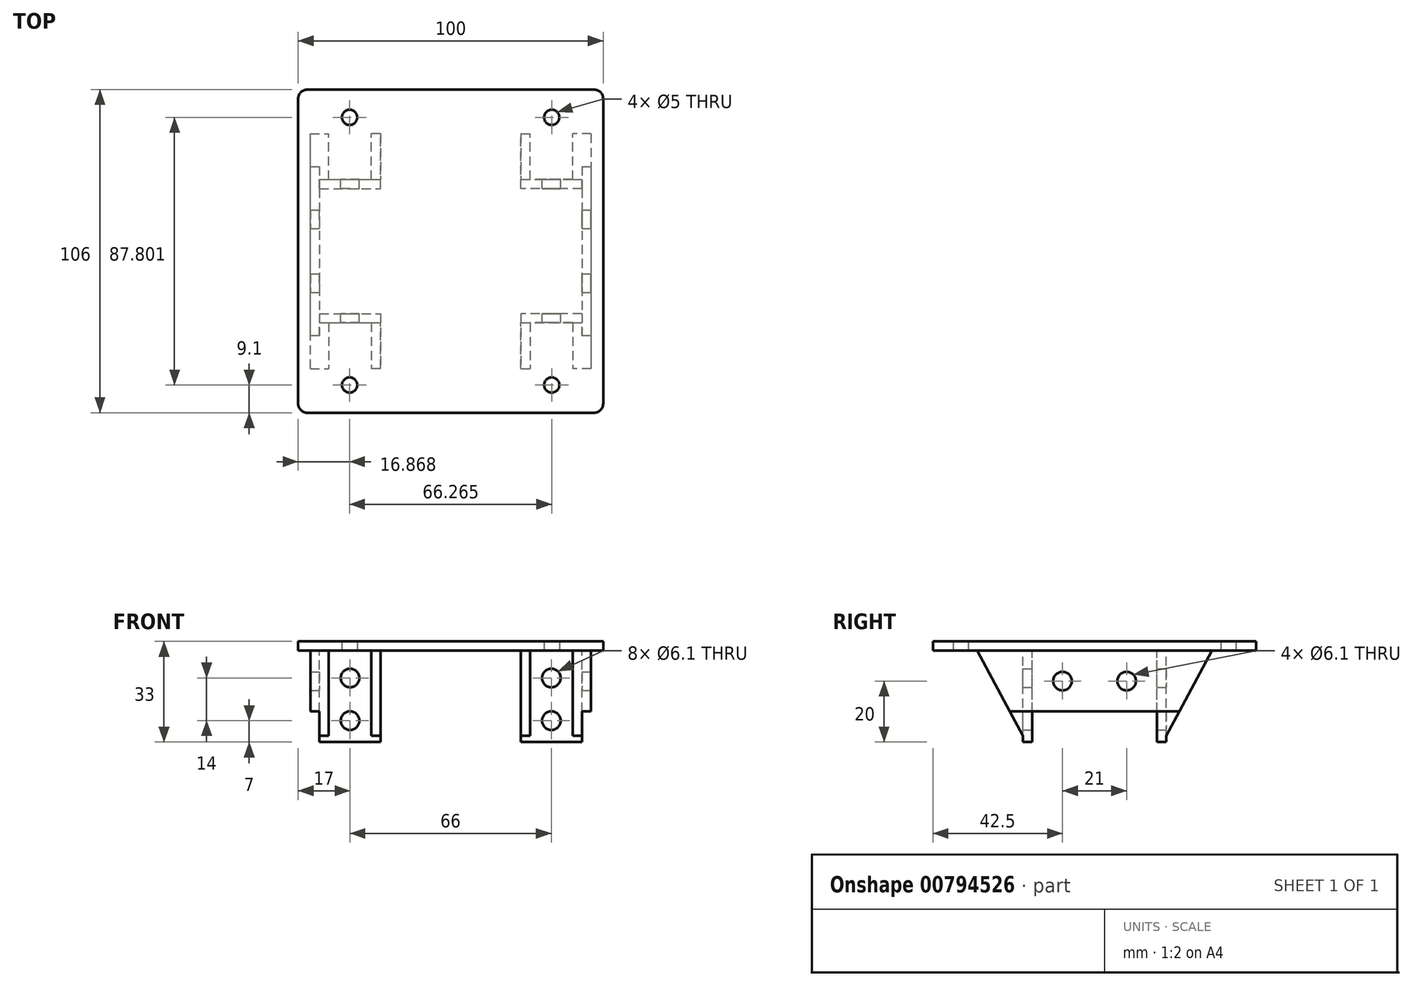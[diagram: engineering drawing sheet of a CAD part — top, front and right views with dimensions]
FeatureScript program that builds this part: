
annotation { "Feature Type Name" : "Feature", "Feature Type Description" : "" }
export const myFeature = defineFeature(function(context is Context, id is Id, definition is map)
    precondition{}
    {
        {
            var Q0;
            Q0=qCreatedBy(makeId("Top.planeOp"),FACE);
            var sketch = newSketch(context, id + "F0", { "sketchPlane" : qUnion([Q0])});
            skLineSegment(sketch, "E0.bottom", {"start": v(40, -53) * mm, "end": v(-40, -53) * mm, "construction": true});
            skLineSegment(sketch, "E0.top", {"start": v(40, 53) * mm, "end": v(-40, 53) * mm, "construction": true});
            skLineSegment(sketch, "E0.left", {"start": v(40, -53) * mm, "end": v(40, 53) * mm, "construction": true});
            skLineSegment(sketch, "E0.right", {"start": v(-40, -53) * mm, "end": v(-40, 53) * mm, "construction": true});
            skPoint(sketch, "E0.middle", {"position": v(0, 0) * mm});
            skLineSegment(sketch, "E1.bottom", {"start": v(50, -53) * mm, "end": v(-50, -53) * mm});
            skLineSegment(sketch, "E1.top", {"start": v(50, 53) * mm, "end": v(-50, 53) * mm});
            skLineSegment(sketch, "E1.left", {"start": v(50, -53) * mm, "end": v(50, 53) * mm});
            skLineSegment(sketch, "E1.right", {"start": v(-50, -53) * mm, "end": v(-50, 53) * mm});
            skLineSegment(sketch, "E2", {"start": v(40, 53) * mm, "end": v(-40, -53) * mm, "construction": true});
            skLineSegment(sketch, "E3", {"start": v(-40, 53) * mm, "end": v(40, -53) * mm, "construction": true});
            skCircle(sketch, "E4", {"center": v(33.13, -43.9) * mm, "radius": 2.5 * mm});
            skCircle(sketch, "E5", {"center": v(-33.13, -43.9) * mm, "radius": 2.5 * mm});
            skCircle(sketch, "E6", {"center": v(-33.13, 43.9) * mm, "radius": 2.5 * mm});
            skCircle(sketch, "E7", {"center": v(33.13, 43.9) * mm, "radius": 2.5 * mm});
            skSolve(sketch);
        }
        {
            var Q0;
            Q0=makeQuery(id+"F0.imprint","IMPRINT",FACE,{"disambiguationData":[TD([[makeQuery(id+"F0.imprint","IMPRINT",EDGE,{"derivedFrom":sQuery(id+"F0.wireOp",EDGE,"E1.bottom")}),-1.0]])]});
            extrude(context, id + "F1", {"entities" : qUnion([Q0]), "depth" : 3 * mm, "offsetDistance" : 25 * mm});
        }
        {
            var Q0;
            Q0=makeQuery(id+"F1.opExtrude","SWEPT_EDGE",EDGE,{"disambiguationData":[OSD([sQuery(id+"F0.wireOp",EDGE,"E1.bottom"),sQuery(id+"F0.wireOp",EDGE,"E1.right")])]});
            var Q1;
            Q1=makeQuery(id+"F1.opExtrude","SWEPT_EDGE",EDGE,{"disambiguationData":[OSD([sQuery(id+"F0.wireOp",EDGE,"E1.top"),sQuery(id+"F0.wireOp",EDGE,"E1.right")])]});
            var Q2;
            Q2=makeQuery(id+"F1.opExtrude","SWEPT_EDGE",EDGE,{"disambiguationData":[OSD([sQuery(id+"F0.wireOp",EDGE,"E1.top"),sQuery(id+"F0.wireOp",EDGE,"E1.left")])]});
            var Q3;
            Q3=makeQuery(id+"F1.opExtrude","SWEPT_EDGE",EDGE,{"disambiguationData":[OSD([sQuery(id+"F0.wireOp",EDGE,"E1.bottom"),sQuery(id+"F0.wireOp",EDGE,"E1.left")])]});
            fillet(context, id + "F2", {"entities" : qUnion([Q0, Q1, Q2, Q3]), "radius" : 3 * mm, "tangentPropagation" : true, "allowEdgeOverflow" : false});
        }
        {
            var Q0;
            Q0=qCreatedBy(makeId("Top.planeOp"),FACE);
            var sketch = newSketch(context, id + "F3", { "sketchPlane" : qUnion([Q0])});
            skLineSegment(sketch, "E8.1", {"start": v(50, -53) * mm, "end": v(-50, -53) * mm});
            skLineSegment(sketch, "E8.2", {"start": v(50, 53) * mm, "end": v(-50, 53) * mm});
            skLineSegment(sketch, "E9", {"start": v(-43, -53) * mm, "end": v(-43, 53) * mm, "construction": true});
            skLineSegment(sketch, "E10", {"start": v(43, -53) * mm, "end": v(43, 53) * mm, "construction": true});
            skLineSegment(sketch, "E11", {"start": v(-43, -20.5) * mm, "end": v(43, -20.5) * mm, "construction": true});
            skLineSegment(sketch, "E12", {"start": v(-43, 20.5) * mm, "end": v(43, 20.5) * mm, "construction": true});
            skLineSegment(sketch, "E13", {"start": v(-33, -20.5) * mm, "end": v(-33, 20.5) * mm, "construction": true});
            skLineSegment(sketch, "E14", {"start": v(33, 20.5) * mm, "end": v(33, -20.5) * mm, "construction": true});
            skLineSegment(sketch, "E15.bottom", {"start": v(-43, 20.5) * mm, "end": v(-23, 20.5) * mm});
            skLineSegment(sketch, "E15.top", {"start": v(-43, 23.5) * mm, "end": v(-23, 23.5) * mm});
            skLineSegment(sketch, "E15.left", {"start": v(-43, 20.5) * mm, "end": v(-43, 23.5) * mm});
            skLineSegment(sketch, "E15.right", {"start": v(-23, 20.5) * mm, "end": v(-23, 23.5) * mm});
            skLineSegment(sketch, "E16.bottom", {"start": v(-43, -20.5) * mm, "end": v(-23, -20.5) * mm});
            skLineSegment(sketch, "E16.top", {"start": v(-43, -23.5) * mm, "end": v(-23, -23.5) * mm});
            skLineSegment(sketch, "E16.left", {"start": v(-43, -20.5) * mm, "end": v(-43, -23.5) * mm});
            skLineSegment(sketch, "E16.right", {"start": v(-23, -20.5) * mm, "end": v(-23, -23.5) * mm});
            skLineSegment(sketch, "E17.bottom", {"start": v(43, -20.5) * mm, "end": v(23, -20.5) * mm});
            skLineSegment(sketch, "E17.top", {"start": v(43, -23.5) * mm, "end": v(23, -23.5) * mm});
            skLineSegment(sketch, "E17.left", {"start": v(43, -20.5) * mm, "end": v(43, -23.5) * mm});
            skLineSegment(sketch, "E17.right", {"start": v(23, -20.5) * mm, "end": v(23, -23.5) * mm});
            skLineSegment(sketch, "E18.bottom", {"start": v(43, 20.5) * mm, "end": v(23, 20.5) * mm});
            skLineSegment(sketch, "E18.top", {"start": v(43, 23.5) * mm, "end": v(23, 23.5) * mm});
            skLineSegment(sketch, "E18.left", {"start": v(43, 20.5) * mm, "end": v(43, 23.5) * mm});
            skLineSegment(sketch, "E18.right", {"start": v(23, 20.5) * mm, "end": v(23, 23.5) * mm});
            skLineSegment(sketch, "E19.bottom", {"start": v(-43, -23.5) * mm, "end": v(-46, -23.5) * mm});
            skLineSegment(sketch, "E19.top", {"start": v(-43, 23.5) * mm, "end": v(-46, 23.5) * mm});
            skLineSegment(sketch, "E19.left", {"start": v(-43, -23.5) * mm, "end": v(-43, 23.5) * mm});
            skLineSegment(sketch, "E19.right", {"start": v(-46, -23.5) * mm, "end": v(-46, 23.5) * mm});
            skLineSegment(sketch, "E20.bottom", {"start": v(43, 23.5) * mm, "end": v(46, 23.5) * mm});
            skLineSegment(sketch, "E20.top", {"start": v(43, -23.5) * mm, "end": v(46, -23.5) * mm});
            skLineSegment(sketch, "E20.left", {"start": v(43, 23.5) * mm, "end": v(43, -23.5) * mm});
            skLineSegment(sketch, "E20.right", {"start": v(46, 23.5) * mm, "end": v(46, -23.5) * mm});
            skLineSegment(sketch, "E21.bottom", {"start": v(-43, 23.5) * mm, "end": v(-40, 23.5) * mm});
            skLineSegment(sketch, "E21.top", {"start": v(-43, 38.5) * mm, "end": v(-40, 38.5) * mm});
            skLineSegment(sketch, "E21.left", {"start": v(-43, 23.5) * mm, "end": v(-43, 38.5) * mm});
            skLineSegment(sketch, "E21.right", {"start": v(-40, 23.5) * mm, "end": v(-40, 38.5) * mm});
            skLineSegment(sketch, "E22.bottom", {"start": v(-23, 23.5) * mm, "end": v(-26, 23.5) * mm});
            skLineSegment(sketch, "E22.top", {"start": v(-23, 38.5) * mm, "end": v(-26, 38.5) * mm});
            skLineSegment(sketch, "E22.left", {"start": v(-23, 23.5) * mm, "end": v(-23, 38.5) * mm});
            skLineSegment(sketch, "E22.right", {"start": v(-26, 23.5) * mm, "end": v(-26, 38.5) * mm});
            skLineSegment(sketch, "E23.bottom", {"start": v(23, 23.5) * mm, "end": v(26, 23.5) * mm});
            skLineSegment(sketch, "E23.top", {"start": v(23, 38.5) * mm, "end": v(26, 38.5) * mm});
            skLineSegment(sketch, "E23.left", {"start": v(23, 23.5) * mm, "end": v(23, 38.5) * mm});
            skLineSegment(sketch, "E23.right", {"start": v(26, 23.5) * mm, "end": v(26, 38.5) * mm});
            skLineSegment(sketch, "E24.bottom", {"start": v(43, 23.5) * mm, "end": v(40, 23.5) * mm});
            skLineSegment(sketch, "E24.top", {"start": v(43, 38.5) * mm, "end": v(40, 38.5) * mm});
            skLineSegment(sketch, "E24.left", {"start": v(43, 23.5) * mm, "end": v(43, 38.5) * mm});
            skLineSegment(sketch, "E24.right", {"start": v(40, 23.5) * mm, "end": v(40, 38.5) * mm});
            skLineSegment(sketch, "E25.bottom", {"start": v(23, -23.5) * mm, "end": v(26, -23.5) * mm});
            skLineSegment(sketch, "E25.top", {"start": v(23, -38.5) * mm, "end": v(26, -38.5) * mm});
            skLineSegment(sketch, "E25.left", {"start": v(23, -23.5) * mm, "end": v(23, -38.5) * mm});
            skLineSegment(sketch, "E25.right", {"start": v(26, -23.5) * mm, "end": v(26, -38.5) * mm});
            skLineSegment(sketch, "E26.bottom", {"start": v(43, -23.5) * mm, "end": v(40, -23.5) * mm});
            skLineSegment(sketch, "E26.top", {"start": v(43, -38.5) * mm, "end": v(40, -38.5) * mm});
            skLineSegment(sketch, "E26.left", {"start": v(43, -23.5) * mm, "end": v(43, -38.5) * mm});
            skLineSegment(sketch, "E26.right", {"start": v(40, -23.5) * mm, "end": v(40, -38.5) * mm});
            skLineSegment(sketch, "E27.bottom", {"start": v(-23, -23.5) * mm, "end": v(-26, -23.5) * mm});
            skLineSegment(sketch, "E27.top", {"start": v(-23, -38.5) * mm, "end": v(-26, -38.5) * mm});
            skLineSegment(sketch, "E27.left", {"start": v(-23, -23.5) * mm, "end": v(-23, -38.5) * mm});
            skLineSegment(sketch, "E27.right", {"start": v(-26, -23.5) * mm, "end": v(-26, -38.5) * mm});
            skLineSegment(sketch, "E28.bottom", {"start": v(-43, -23.5) * mm, "end": v(-40, -23.5) * mm});
            skLineSegment(sketch, "E28.top", {"start": v(-43, -38.5) * mm, "end": v(-40, -38.5) * mm});
            skLineSegment(sketch, "E28.left", {"start": v(-43, -23.5) * mm, "end": v(-43, -38.5) * mm});
            skLineSegment(sketch, "E28.right", {"start": v(-40, -23.5) * mm, "end": v(-40, -38.5) * mm});
            skSolve(sketch);
        }
        {
            var Q0;
            Q0=makeQuery(id+"F3.imprint","IMPRINT",FACE,{"disambiguationData":[TD([[makeQuery(id+"F3.imprint","IMPRINT",EDGE,{"derivedFrom":sQuery(id+"F3.wireOp",EDGE,"E16.bottom")}),-1.0]])]});
            var Q1;
            Q1=makeQuery(id+"F3.imprint","IMPRINT",FACE,{"disambiguationData":[TD([[makeQuery(id+"F3.imprint","IMPRINT",EDGE,{"derivedFrom":sQuery(id+"F3.wireOp",EDGE,"E15.bottom")}),1.0]])]});
            var Q2;
            Q2=makeQuery(id+"F3.imprint","IMPRINT",FACE,{"disambiguationData":[TD([[makeQuery(id+"F3.imprint","IMPRINT",EDGE,{"derivedFrom":sQuery(id+"F3.wireOp",EDGE,"E18.bottom")}),-1.0]])]});
            var Q3;
            Q3=makeQuery(id+"F3.imprint","IMPRINT",FACE,{"disambiguationData":[TD([[makeQuery(id+"F3.imprint","IMPRINT",EDGE,{"derivedFrom":sQuery(id+"F3.wireOp",EDGE,"E17.bottom")}),1.0]])]});
            extrude(context, id + "F4", {"entities" : qUnion([Q0, Q1, Q2, Q3]), "operationType" : NewBodyOperationType.ADD, "oppositeDirection" : true, "depth" : 28 * mm, "offsetDistance" : 25 * mm});
        }
        {
            var Q0;
            Q0=makeQuery(id+"F3.imprint","IMPRINT",FACE,{"disambiguationData":[TD([[makeQuery(id+"F3.imprint","IMPRINT",EDGE,{"derivedFrom":sQuery(id+"F3.wireOp",EDGE,"E17.left")}),1.0]])]});
            var Q1;
            Q1=makeQuery(id+"F3.imprint","IMPRINT",FACE,{"disambiguationData":[TD([[makeQuery(id+"F3.imprint","IMPRINT",EDGE,{"derivedFrom":sQuery(id+"F3.wireOp",EDGE,"E15.left")}),1.0]])]});
            extrude(context, id + "F5", {"entities" : qUnion([Q0, Q1]), "operationType" : NewBodyOperationType.ADD, "oppositeDirection" : true, "depth" : 20 * mm, "offsetDistance" : 25 * mm});
        }
        {
            var Q0;
            Q0=makeQuery(id+"F3.imprint","IMPRINT",FACE,{"disambiguationData":[TD([[makeQuery(id+"F3.imprint","IMPRINT",EDGE,{"derivedFrom":sQuery(id+"F3.wireOp",EDGE,"E21.top")}),-1.0]])]});
            var Q1;
            Q1=makeQuery(id+"F3.imprint","IMPRINT",FACE,{"disambiguationData":[TD([[makeQuery(id+"F3.imprint","IMPRINT",EDGE,{"derivedFrom":sQuery(id+"F3.wireOp",EDGE,"E22.top")}),1.0]])]});
            var Q2;
            Q2=makeQuery(id+"F3.imprint","IMPRINT",FACE,{"disambiguationData":[TD([[makeQuery(id+"F3.imprint","IMPRINT",EDGE,{"derivedFrom":sQuery(id+"F3.wireOp",EDGE,"E23.top")}),-1.0]])]});
            var Q3;
            Q3=makeQuery(id+"F3.imprint","IMPRINT",FACE,{"disambiguationData":[TD([[makeQuery(id+"F3.imprint","IMPRINT",EDGE,{"derivedFrom":sQuery(id+"F3.wireOp",EDGE,"E24.top")}),1.0]])]});
            var Q4;
            Q4=makeQuery(id+"F3.imprint","IMPRINT",FACE,{"disambiguationData":[TD([[makeQuery(id+"F3.imprint","IMPRINT",EDGE,{"derivedFrom":sQuery(id+"F3.wireOp",EDGE,"E28.top")}),1.0]])]});
            var Q5;
            Q5=makeQuery(id+"F3.imprint","IMPRINT",FACE,{"disambiguationData":[TD([[makeQuery(id+"F3.imprint","IMPRINT",EDGE,{"derivedFrom":sQuery(id+"F3.wireOp",EDGE,"E27.top")}),-1.0]])]});
            var Q6;
            Q6=makeQuery(id+"F3.imprint","IMPRINT",FACE,{"disambiguationData":[TD([[makeQuery(id+"F3.imprint","IMPRINT",EDGE,{"derivedFrom":sQuery(id+"F3.wireOp",EDGE,"E25.top")}),1.0]])]});
            var Q7;
            Q7=makeQuery(id+"F3.imprint","IMPRINT",FACE,{"disambiguationData":[TD([[makeQuery(id+"F3.imprint","IMPRINT",EDGE,{"derivedFrom":sQuery(id+"F3.wireOp",EDGE,"E26.top")}),-1.0]])]});
            extrude(context, id + "F6", {"entities" : qUnion([Q0, Q1, Q2, Q3, Q4, Q5, Q6, Q7]), "operationType" : NewBodyOperationType.ADD, "oppositeDirection" : true, "depth" : 28 * mm, "offsetDistance" : 25 * mm});
        }
        {
            var Q0;
            {var subQ1=sQuery(id+"F3.wireOp",EDGE,"E19.bottom");var subQ2=sQuery(id+"F3.wireOp",EDGE,"E16.left");Q0=makeQuery(id+"F6.boolean.opBoolean","SPLIT",FACE,{"disambiguationData":[TD([makeQuery(id+"F4.opExtrude","SWEPT_FACE",FACE,{"disambiguationData":[OSD([subQ2])]})])],"derivedFrom":makeQuery(id+"F5.boolean.opBoolean","MERGE",FACE,{"derivedFrom":[makeQuery(id+"F4.opExtrude","SWEPT_FACE",FACE,{"disambiguationData":[OSD([sQuery(id+"F3.wireOp",EDGE,"E16.top")])]}),makeQuery(id+"F5.opExtrude","SWEPT_FACE",FACE,{"disambiguationData":[OSD([subQ1])]})]})});}
            var Q1;
            {var subQ1=sQuery(id+"F3.wireOp",EDGE,"E20.top");var subQ2=sQuery(id+"F3.wireOp",EDGE,"E17.left");Q1=makeQuery(id+"F6.boolean.opBoolean","SPLIT",FACE,{"disambiguationData":[TD([makeQuery(id+"F4.opExtrude","SWEPT_FACE",FACE,{"disambiguationData":[OSD([subQ2])]})])],"derivedFrom":makeQuery(id+"F5.boolean.opBoolean","MERGE",FACE,{"derivedFrom":[makeQuery(id+"F4.opExtrude","SWEPT_FACE",FACE,{"disambiguationData":[OSD([sQuery(id+"F3.wireOp",EDGE,"E17.top")])]}),makeQuery(id+"F5.opExtrude","SWEPT_FACE",FACE,{"disambiguationData":[OSD([subQ1])]})]})});}
            var Q2;
            Q2=makeQuery(id+"F6.opExtrude","SWEPT_FACE",FACE,{"disambiguationData":[OSD([sQuery(id+"F3.wireOp",EDGE,"E28.top")])]});
            var Q3;
            Q3=makeQuery(id+"F6.opExtrude","SWEPT_FACE",FACE,{"disambiguationData":[OSD([sQuery(id+"F3.wireOp",EDGE,"E21.top")])]});
            extrude(context, id + "F7", {"entities" : qUnion([Q0, Q1]), "operationType" : NewBodyOperationType.ADD, "endBound" : BoundingType.UP_TO_SURFACE, "depth" : 25 * mm, "endBoundEntityFace" : qUnion([Q2]), "offsetDistance" : 25 * mm, "hasSecondDirection" : true, "secondDirectionBound" : SecondDirectionBoundingType.UP_TO_SURFACE, "secondDirectionOppositeDirection" : true, "secondDirectionDepth" : 25 * mm, "secondDirectionBoundEntityFace" : qUnion([Q3])});
        }
        {
            var Q0;
            Q0=makeQuery(id+"F6.opExtrude","SWEPT_FACE",FACE,{"disambiguationData":[OSD([sQuery(id+"F3.wireOp",EDGE,"E22.right")])]});
            var sketch = newSketch(context, id + "F8", { "sketchPlane" : qUnion([Q0])});
            skLineSegment(sketch, "E29", {"start": v(-38.5, 0) * mm, "end": v(-23.5, -28) * mm});
            skSolve(sketch);
        }
        {
            var Q0;
            Q0=makeQuery(id+"F8.imprint","IMPRINT",FACE,{"disambiguationData":[TD([[makeQuery(id+"F8.imprint","IMPRINT",EDGE,{"derivedFrom":sQuery(id+"F8.wireOp",EDGE,"E29")}),-1.0]])]});
            var Q1;
            {var subQ0=sQuery(id+"F3.wireOp",EDGE,"E19.right");Q1=makeQuery(id+"F7.boolean.opBoolean","MERGE",FACE,{"derivedFrom":[makeQuery(id+"F5.opExtrude","SWEPT_FACE",FACE,{"disambiguationData":[OSD([subQ0])]}),makeQuery(id+"F7.opExtrude","SWEPT_FACE",FACE,{"disambiguationData":[OSD([sQuery(id+"F3.wireOp",EDGE,"E19.bottom"),subQ0])]})]});}
            var Q2;
            {var subQ0=sQuery(id+"F3.wireOp",EDGE,"E20.right");Q2=makeQuery(id+"F7.boolean.opBoolean","MERGE",FACE,{"derivedFrom":[makeQuery(id+"F5.opExtrude","SWEPT_FACE",FACE,{"disambiguationData":[OSD([subQ0])]}),makeQuery(id+"F7.opExtrude","SWEPT_FACE",FACE,{"disambiguationData":[OSD([sQuery(id+"F3.wireOp",EDGE,"E20.top"),subQ0])]})]});}
            extrude(context, id + "F9", {"entities" : qUnion([Q0]), "operationType" : NewBodyOperationType.REMOVE, "endBound" : BoundingType.UP_TO_SURFACE, "depth" : 25 * mm, "endBoundEntityFace" : qUnion([Q1]), "offsetDistance" : 25 * mm, "hasSecondDirection" : true, "secondDirectionBound" : SecondDirectionBoundingType.UP_TO_SURFACE, "secondDirectionOppositeDirection" : true, "secondDirectionDepth" : 25 * mm, "secondDirectionBoundEntityFace" : qUnion([Q2])});
        }
        {
            var Q0;
            Q0=makeQuery(id+"F6.opExtrude","SWEPT_FACE",FACE,{"disambiguationData":[OSD([sQuery(id+"F3.wireOp",EDGE,"E27.right")])]});
            var sketch = newSketch(context, id + "F10", { "sketchPlane" : qUnion([Q0])});
            skLineSegment(sketch, "E30", {"start": v(23.5, -28) * mm, "end": v(38.5, 0) * mm});
            skSolve(sketch);
        }
        {
            var Q0;
            Q0=makeQuery(id+"F10.imprint","IMPRINT",FACE,{"disambiguationData":[TD([[makeQuery(id+"F10.imprint","IMPRINT",EDGE,{"derivedFrom":sQuery(id+"F10.wireOp",EDGE,"E30")}),-1.0]])]});
            var Q1;
            {var subQ0=sQuery(id+"F3.wireOp",EDGE,"E19.right");Q1=makeQuery(id+"F7.boolean.opBoolean","MERGE",FACE,{"derivedFrom":[makeQuery(id+"F5.opExtrude","SWEPT_FACE",FACE,{"disambiguationData":[OSD([subQ0])]}),makeQuery(id+"F7.opExtrude","SWEPT_FACE",FACE,{"disambiguationData":[OSD([sQuery(id+"F3.wireOp",EDGE,"E19.bottom"),subQ0])]})]});}
            var Q2;
            {var subQ0=sQuery(id+"F3.wireOp",EDGE,"E20.right");Q2=makeQuery(id+"F7.boolean.opBoolean","MERGE",FACE,{"derivedFrom":[makeQuery(id+"F5.opExtrude","SWEPT_FACE",FACE,{"disambiguationData":[OSD([subQ0])]}),makeQuery(id+"F7.opExtrude","SWEPT_FACE",FACE,{"disambiguationData":[OSD([sQuery(id+"F3.wireOp",EDGE,"E20.top"),subQ0])]})]});}
            extrude(context, id + "F11", {"entities" : qUnion([Q0]), "operationType" : NewBodyOperationType.REMOVE, "endBound" : BoundingType.UP_TO_SURFACE, "depth" : 25 * mm, "endBoundEntityFace" : qUnion([Q1]), "offsetDistance" : 25 * mm, "hasSecondDirection" : true, "secondDirectionBound" : SecondDirectionBoundingType.UP_TO_SURFACE, "secondDirectionOppositeDirection" : true, "secondDirectionDepth" : 25 * mm, "secondDirectionBoundEntityFace" : qUnion([Q2])});
        }
        {
            var Q0;
            {var subQ0=sQuery(id+"F3.wireOp",EDGE,"E21.right");var subQ1=sQuery(id+"F3.wireOp",EDGE,"E15.top");Q0=makeQuery(id+"F6.boolean.opBoolean","SPLIT",FACE,{"disambiguationData":[TD([makeQuery(id+"F6.opExtrude","SWEPT_FACE",FACE,{"disambiguationData":[OSD([subQ0])]})])],"derivedFrom":makeQuery(id+"F5.boolean.opBoolean","MERGE",FACE,{"derivedFrom":[makeQuery(id+"F4.opExtrude","SWEPT_FACE",FACE,{"disambiguationData":[OSD([subQ1])]}),makeQuery(id+"F5.opExtrude","SWEPT_FACE",FACE,{"disambiguationData":[OSD([sQuery(id+"F3.wireOp",EDGE,"E19.top")])]})]})});}
            var sketch = newSketch(context, id + "F12", { "sketchPlane" : qUnion([Q0])});
            skLineSegment(sketch, "E31", {"start": v(33, -28) * mm, "end": v(33, 0) * mm, "construction": true});
            skCircle(sketch, "E32", {"center": v(33, -23) * mm, "radius": 3.05 * mm});
            skCircle(sketch, "E33", {"center": v(33, -9) * mm, "radius": 3.05 * mm});
            skSolve(sketch);
        }
        {
            var Q0;
            {var subQ1=sQuery(id+"F3.wireOp",EDGE,"E18.top");var subQ2=sQuery(id+"F3.wireOp",EDGE,"E23.right");Q0=makeQuery(id+"F6.boolean.opBoolean","SPLIT",FACE,{"disambiguationData":[TD([makeQuery(id+"F6.opExtrude","SWEPT_FACE",FACE,{"disambiguationData":[OSD([subQ2])]})])],"derivedFrom":makeQuery(id+"F5.boolean.opBoolean","MERGE",FACE,{"derivedFrom":[makeQuery(id+"F4.opExtrude","SWEPT_FACE",FACE,{"disambiguationData":[OSD([subQ1])]}),makeQuery(id+"F5.opExtrude","SWEPT_FACE",FACE,{"disambiguationData":[OSD([sQuery(id+"F3.wireOp",EDGE,"E20.bottom")])]})]})});}
            var sketch = newSketch(context, id + "F13", { "sketchPlane" : qUnion([Q0])});
            skLineSegment(sketch, "E34", {"start": v(-33, 0) * mm, "end": v(-33, -28) * mm, "construction": true});
            skCircle(sketch, "E35", {"center": v(-33, -23) * mm, "radius": 3.05 * mm});
            skCircle(sketch, "E36", {"center": v(-33, -9) * mm, "radius": 3.05 * mm});
            skSolve(sketch);
        }
        {
            var Q0;
            Q0=makeQuery(id+"F12.imprint","IMPRINT",FACE,{"disambiguationData":[TD([[makeQuery(id+"F12.imprint","IMPRINT",EDGE,{"derivedFrom":sQuery(id+"F12.wireOp",EDGE,"E32")}),1.0]])]});
            var Q1;
            Q1=makeQuery(id+"F12.imprint","IMPRINT",FACE,{"disambiguationData":[TD([[makeQuery(id+"F12.imprint","IMPRINT",EDGE,{"derivedFrom":sQuery(id+"F12.wireOp",EDGE,"E33")}),1.0]])]});
            var Q2;
            Q2=makeQuery(id+"F13.imprint","IMPRINT",FACE,{"disambiguationData":[TD([[makeQuery(id+"F13.imprint","IMPRINT",EDGE,{"derivedFrom":sQuery(id+"F13.wireOp",EDGE,"E36")}),1.0]])]});
            var Q3;
            Q3=makeQuery(id+"F13.imprint","IMPRINT",FACE,{"disambiguationData":[TD([[makeQuery(id+"F13.imprint","IMPRINT",EDGE,{"derivedFrom":sQuery(id+"F13.wireOp",EDGE,"E35")}),1.0]])]});
            var Q4;
            {var subQ0=sQuery(id+"F3.wireOp",EDGE,"E27.right");var subQ1=sQuery(id+"F3.wireOp",EDGE,"E16.top");Q4=makeQuery(id+"F6.boolean.opBoolean","SPLIT",FACE,{"disambiguationData":[TD([makeQuery(id+"F6.opExtrude","SWEPT_FACE",FACE,{"disambiguationData":[OSD([subQ0])]})])],"derivedFrom":makeQuery(id+"F5.boolean.opBoolean","MERGE",FACE,{"derivedFrom":[makeQuery(id+"F4.opExtrude","SWEPT_FACE",FACE,{"disambiguationData":[OSD([subQ1])]}),makeQuery(id+"F5.opExtrude","SWEPT_FACE",FACE,{"disambiguationData":[OSD([sQuery(id+"F3.wireOp",EDGE,"E19.bottom")])]})]})});}
            extrude(context, id + "F14", {"entities" : qUnion([Q0, Q1, Q2, Q3]), "operationType" : NewBodyOperationType.REMOVE, "endBound" : BoundingType.UP_TO_SURFACE, "oppositeDirection" : true, "depth" : 25 * mm, "endBoundEntityFace" : qUnion([Q4]), "offsetDistance" : 25 * mm});
        }
        {
            var Q0;
            Q0=makeQuery(id+"F5.opExtrude","SWEPT_FACE",FACE,{"disambiguationData":[OSD([sQuery(id+"F3.wireOp",EDGE,"E15.left"),sQuery(id+"F3.wireOp",EDGE,"E16.left"),sQuery(id+"F3.wireOp",EDGE,"E19.left")])]});
            var sketch = newSketch(context, id + "F15", { "sketchPlane" : qUnion([Q0])});
            skLineSegment(sketch, "E37", {"start": v(-10.5, 0) * mm, "end": v(-10.5, -20) * mm, "construction": true});
            skLineSegment(sketch, "E38", {"start": v(10.5, 0) * mm, "end": v(10.5, -20) * mm, "construction": true});
            skCircle(sketch, "E39", {"center": v(10.5, -10) * mm, "radius": 3.05 * mm});
            skCircle(sketch, "E40", {"center": v(-10.5, -10) * mm, "radius": 3.05 * mm});
            skSolve(sketch);
        }
        {
            var Q0;
            Q0=makeQuery(id+"F15.imprint","IMPRINT",FACE,{"disambiguationData":[TD([[makeQuery(id+"F15.imprint","IMPRINT",EDGE,{"derivedFrom":sQuery(id+"F15.wireOp",EDGE,"E39")}),1.0]])]});
            var Q1;
            Q1=makeQuery(id+"F15.imprint","IMPRINT",FACE,{"disambiguationData":[TD([[makeQuery(id+"F15.imprint","IMPRINT",EDGE,{"derivedFrom":sQuery(id+"F15.wireOp",EDGE,"E40")}),1.0]])]});
            var Q2;
            {var subQ0=sQuery(id+"F3.wireOp",EDGE,"E19.right");Q2=makeQuery(id+"F7.boolean.opBoolean","MERGE",FACE,{"derivedFrom":[makeQuery(id+"F5.opExtrude","SWEPT_FACE",FACE,{"disambiguationData":[OSD([subQ0])]}),makeQuery(id+"F7.opExtrude","SWEPT_FACE",FACE,{"disambiguationData":[OSD([sQuery(id+"F3.wireOp",EDGE,"E19.bottom"),subQ0])]})]});}
            var Q3;
            {var subQ0=sQuery(id+"F3.wireOp",EDGE,"E20.right");Q3=makeQuery(id+"F7.boolean.opBoolean","MERGE",FACE,{"derivedFrom":[makeQuery(id+"F5.opExtrude","SWEPT_FACE",FACE,{"disambiguationData":[OSD([subQ0])]}),makeQuery(id+"F7.opExtrude","SWEPT_FACE",FACE,{"disambiguationData":[OSD([sQuery(id+"F3.wireOp",EDGE,"E20.top"),subQ0])]})]});}
            extrude(context, id + "F16", {"entities" : qUnion([Q0, Q1]), "operationType" : NewBodyOperationType.REMOVE, "endBound" : BoundingType.UP_TO_SURFACE, "oppositeDirection" : true, "depth" : 25 * mm, "endBoundEntityFace" : qUnion([Q2]), "offsetDistance" : 25 * mm, "hasSecondDirection" : true, "secondDirectionBound" : SecondDirectionBoundingType.UP_TO_SURFACE, "secondDirectionOppositeDirection" : false, "secondDirectionDepth" : 25 * mm, "secondDirectionBoundEntityFace" : qUnion([Q3])});
        }
        {
            var Q0;
            {var subQ0=sQuery(id+"F3.wireOp",EDGE,"E17.top");Q0=makeQuery(id+"F6.boolean.opBoolean","MERGE",FACE,{"derivedFrom":[makeQuery(id+"F4.opExtrude","CAP_FACE",FACE,{"disambiguationData":[OSD([sQuery(id+"F3.wireOp",EDGE,"E17.bottom"),subQ0,sQuery(id+"F3.wireOp",EDGE,"E17.left"),sQuery(id+"F3.wireOp",EDGE,"E17.right")])],"isStart":false}),makeQuery(id+"F6.opExtrude","CAP_FACE",FACE,{"disambiguationData":[OSD([subQ0,sQuery(id+"F3.wireOp",EDGE,"E25.top"),sQuery(id+"F3.wireOp",EDGE,"E25.left"),sQuery(id+"F3.wireOp",EDGE,"E25.right")])],"isStart":false}),makeQuery(id+"F6.opExtrude","CAP_FACE",FACE,{"disambiguationData":[OSD([subQ0,sQuery(id+"F3.wireOp",EDGE,"E26.top"),sQuery(id+"F3.wireOp",EDGE,"E26.left"),sQuery(id+"F3.wireOp",EDGE,"E26.right")])],"isStart":false})]});}
            var Q1;
            {var subQ0=sQuery(id+"F3.wireOp",EDGE,"E16.top");Q1=makeQuery(id+"F6.boolean.opBoolean","MERGE",FACE,{"derivedFrom":[makeQuery(id+"F4.opExtrude","CAP_FACE",FACE,{"disambiguationData":[OSD([sQuery(id+"F3.wireOp",EDGE,"E16.bottom"),subQ0,sQuery(id+"F3.wireOp",EDGE,"E16.left"),sQuery(id+"F3.wireOp",EDGE,"E16.right")])],"isStart":false}),makeQuery(id+"F6.opExtrude","CAP_FACE",FACE,{"disambiguationData":[OSD([subQ0,sQuery(id+"F3.wireOp",EDGE,"E28.top"),sQuery(id+"F3.wireOp",EDGE,"E28.left"),sQuery(id+"F3.wireOp",EDGE,"E28.right")])],"isStart":false}),makeQuery(id+"F6.opExtrude","CAP_FACE",FACE,{"disambiguationData":[OSD([subQ0,sQuery(id+"F3.wireOp",EDGE,"E27.top"),sQuery(id+"F3.wireOp",EDGE,"E27.left"),sQuery(id+"F3.wireOp",EDGE,"E27.right")])],"isStart":false})]});}
            var Q2;
            {var subQ0=sQuery(id+"F3.wireOp",EDGE,"E15.top");Q2=makeQuery(id+"F6.boolean.opBoolean","MERGE",FACE,{"derivedFrom":[makeQuery(id+"F4.opExtrude","CAP_FACE",FACE,{"disambiguationData":[OSD([sQuery(id+"F3.wireOp",EDGE,"E15.bottom"),subQ0,sQuery(id+"F3.wireOp",EDGE,"E15.left"),sQuery(id+"F3.wireOp",EDGE,"E15.right")])],"isStart":false}),makeQuery(id+"F6.opExtrude","CAP_FACE",FACE,{"disambiguationData":[OSD([subQ0,sQuery(id+"F3.wireOp",EDGE,"E22.top"),sQuery(id+"F3.wireOp",EDGE,"E22.left"),sQuery(id+"F3.wireOp",EDGE,"E22.right")])],"isStart":false}),makeQuery(id+"F6.opExtrude","CAP_FACE",FACE,{"disambiguationData":[OSD([subQ0,sQuery(id+"F3.wireOp",EDGE,"E21.top"),sQuery(id+"F3.wireOp",EDGE,"E21.left"),sQuery(id+"F3.wireOp",EDGE,"E21.right")])],"isStart":false})]});}
            var Q3;
            {var subQ0=sQuery(id+"F3.wireOp",EDGE,"E18.top");Q3=makeQuery(id+"F6.boolean.opBoolean","MERGE",FACE,{"derivedFrom":[makeQuery(id+"F4.opExtrude","CAP_FACE",FACE,{"disambiguationData":[OSD([sQuery(id+"F3.wireOp",EDGE,"E18.bottom"),subQ0,sQuery(id+"F3.wireOp",EDGE,"E18.left"),sQuery(id+"F3.wireOp",EDGE,"E18.right")])],"isStart":false}),makeQuery(id+"F6.opExtrude","CAP_FACE",FACE,{"disambiguationData":[OSD([subQ0,sQuery(id+"F3.wireOp",EDGE,"E24.top"),sQuery(id+"F3.wireOp",EDGE,"E24.left"),sQuery(id+"F3.wireOp",EDGE,"E24.right")])],"isStart":false}),makeQuery(id+"F6.opExtrude","CAP_FACE",FACE,{"disambiguationData":[OSD([subQ0,sQuery(id+"F3.wireOp",EDGE,"E23.top"),sQuery(id+"F3.wireOp",EDGE,"E23.left"),sQuery(id+"F3.wireOp",EDGE,"E23.right")])],"isStart":false})]});}
            extrude(context, id + "F17", {"entities" : qUnion([Q0, Q1, Q2, Q3]), "operationType" : NewBodyOperationType.ADD, "depth" : 2 * mm, "offsetDistance" : 25 * mm});
        }
    });
